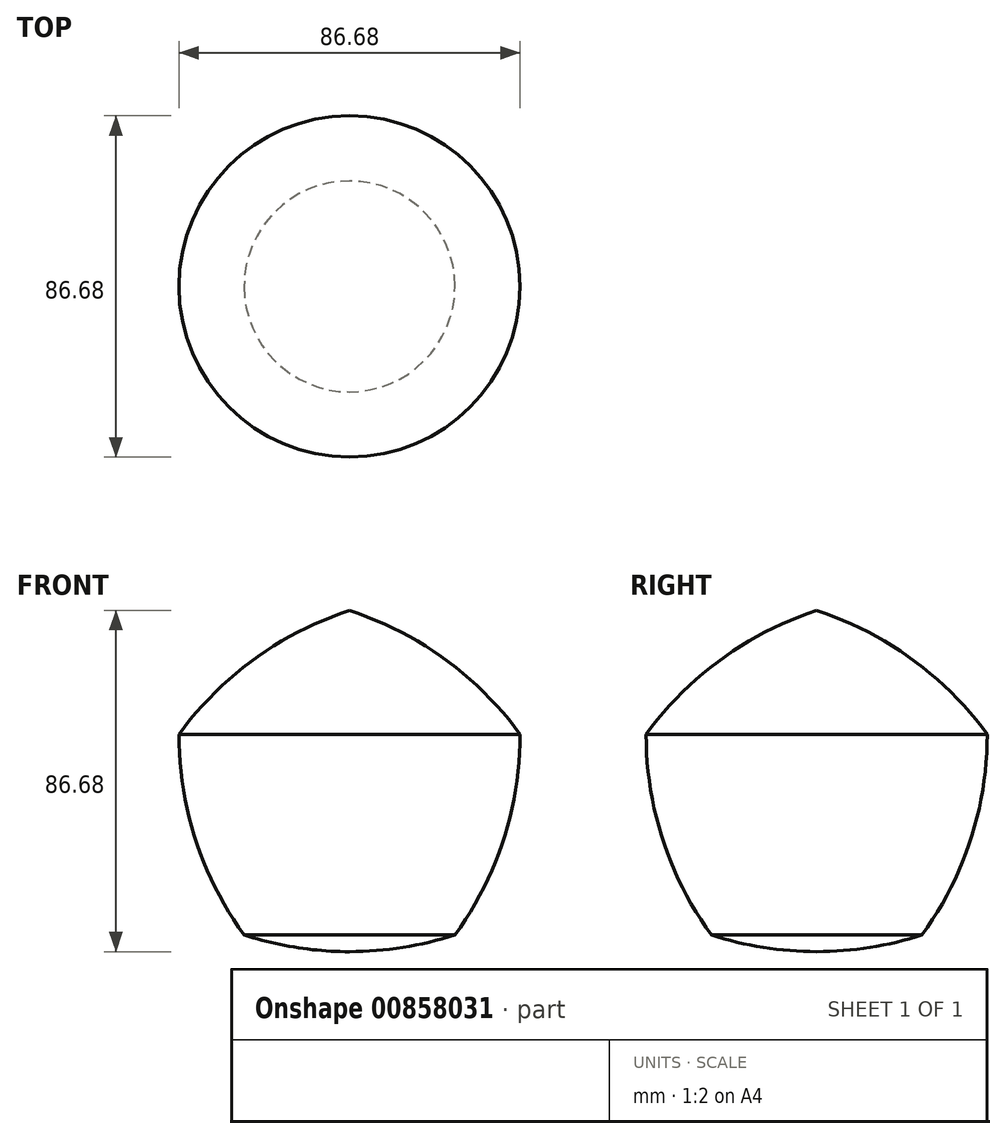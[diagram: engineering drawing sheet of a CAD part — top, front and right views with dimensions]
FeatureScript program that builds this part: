
annotation { "Feature Type Name" : "Feature", "Feature Type Description" : "" }
export const myFeature = defineFeature(function(context is Context, id is Id, definition is map)
    precondition{}
    {
        {
            var Q0;
            Q0=qCreatedBy(makeId("Front.planeOp"),FACE);
            var sketch = newSketch(context, id + "F0", { "sketchPlane" : qUnion([Q0])});
            skPoint(sketch, "E0.0.midPoint", {"position": v(0, -36.87) * mm});
            skCircle(sketch, "E1", {"center": v(-43.34, 14.08) * mm, "radius": 86.68 * mm});
            skCircle(sketch, "E2", {"center": v(0, 45.57) * mm, "radius": 86.68 * mm});
            skCircle(sketch, "E3", {"center": v(43.34, 14.08) * mm, "radius": 86.68 * mm});
            skCircle(sketch, "E4", {"center": v(26.78, -36.87) * mm, "radius": 86.68 * mm});
            skCircle(sketch, "E5", {"center": v(-26.78, -36.87) * mm, "radius": 86.68 * mm});
            skLineSegment(sketch, "E6", {"start": v(0, 45.57) * mm, "end": v(0, -41.1) * mm});
            skSolve(sketch);
        }
        {
            var Q0;
            {var subQ0=sQuery(id+"F0.wireOp",EDGE,"E6");Q0=makeQuery(id+"F0.imprint","IMPRINT",FACE,{"disambiguationData":[TD([[makeQuery(id+"F0.imprint","IMPRINT",EDGE,{"derivedFrom":subQ0}),-1.0]])]});}
            var Q1;
            Q1=sQuery(id+"F0.wireOp",EDGE,"E6");
            revolve(context, id + "F1", {"surfaceOperationType" : NewSurfaceOperationType.NEW, "entities" : qUnion([Q0]), "axis" : qUnion([Q1]), "revolveType" : RevolveType.FULL});
        }
    });
